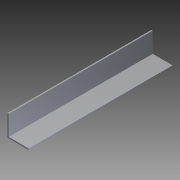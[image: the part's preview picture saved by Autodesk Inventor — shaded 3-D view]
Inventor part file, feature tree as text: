
AUTODESK INVENTOR PART (.ipt)
format: ipt  version: 2012 (Build 160160000, 160)  size: 74,240 bytes
history: native  units: in
note: dims shown in document units (in); Inventor stores cm internally (conversion verified against a paired STEP export)
features: extrude x1, sketch x1
ambient origin geometry x8: Origin, YZ Plane, XZ Plane, XY Plane, X Axis, Y Axis, Z Axis, Center Point
bodies: Solid1 (feature_tree)
feature tree (2):
  extrude  "Extrusion1"  Depth=0.0625in
  sketch  "Sketch1"  dims[d0=0.0625in d1=0.0625in d2=1.0in d3=1.0in d4=6.75in d5=0.0in]
